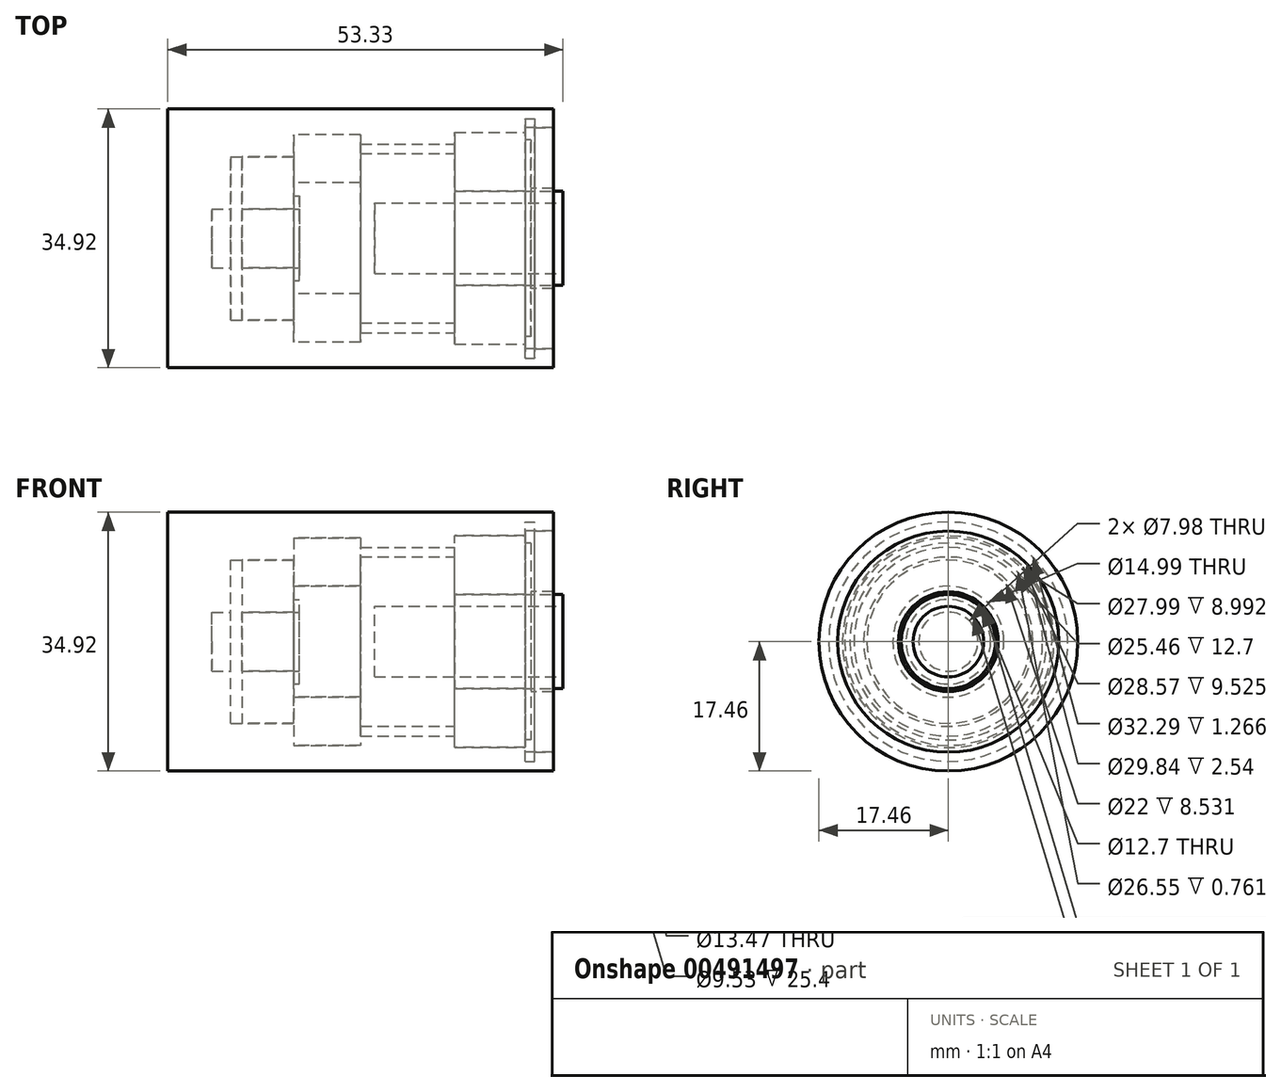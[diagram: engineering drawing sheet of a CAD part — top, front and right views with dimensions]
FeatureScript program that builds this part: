
annotation { "Feature Type Name" : "Feature", "Feature Type Description" : "" }
export const myFeature = defineFeature(function(context is Context, id is Id, definition is map)
    precondition{}
    {
        {
            var Q0;
            Q0=qCreatedBy(makeId("Front.planeOp"),FACE);
            var sketch = newSketch(context, id + "F0", { "sketchPlane" : qUnion([Q0])});
            skLineSegment(sketch, "E0.bottom", {"start": v(0, 0) * mm, "end": v(9.53, 0) * mm});
            skLineSegment(sketch, "E0.top", {"start": v(0, 14.29) * mm, "end": v(9.52, 14.29) * mm});
            skLineSegment(sketch, "E1.bottom", {"start": v(0, 0) * mm, "end": v(-12.7, 0) * mm});
            skLineSegment(sketch, "E1.top", {"start": v(0, 11.43) * mm, "end": v(-12.7, 11.43) * mm});
            skLineSegment(sketch, "E2.bottom", {"start": v(-12.7, 0) * mm, "end": v(-21.7, 0) * mm});
            skLineSegment(sketch, "E2.top", {"start": v(-12.7, 14) * mm, "end": v(-21.7, 14) * mm});
            skLineSegment(sketch, "E3.bottom", {"start": v(-21.7, 0) * mm, "end": v(-26.7, 0) * mm});
            skLineSegment(sketch, "E4.bottom", {"start": v(9.53, 0) * mm, "end": v(14.6, 0) * mm});
            skLineSegment(sketch, "E4.top", {"start": v(9.53, 6.35) * mm, "end": v(14.6, 6.35) * mm});
            skLineSegment(sketch, "E4.right", {"start": v(14.6, 0) * mm, "end": v(14.6, 6.35) * mm});
            skLineSegment(sketch, "E5", {"start": v(-12.7, 7.5) * mm, "end": v(-21.7, 7.5) * mm});
            skLineSegment(sketch, "E6", {"start": v(9.52, 14.29) * mm, "end": v(9.53, 6.35) * mm});
            skLineSegment(sketch, "E7", {"start": v(-12.7, 14) * mm, "end": v(-12.7, 7.5) * mm});
            skLineSegment(sketch, "E8", {"start": v(-21.7, 14) * mm, "end": v(-21.7, 3.99) * mm});
            skLineSegment(sketch, "E9", {"start": v(-27.69, 11) * mm, "end": v(-21.7, 11) * mm});
            skLineSegment(sketch, "E10", {"start": v(-26.7, 0) * mm, "end": v(-27.69, 0) * mm});
            skLineSegment(sketch, "E11", {"start": v(0, 14.29) * mm, "end": v(0, 6.35) * mm});
            skLineSegment(sketch, "E12", {"start": v(0, 6.35) * mm, "end": v(9.53, 6.35) * mm});
            skLineSegment(sketch, "E13", {"start": v(13.33, 7.5) * mm, "end": v(13.33, 17.46) * mm});
            skLineSegment(sketch, "E14", {"start": v(-32.78, 0) * mm, "end": v(-27.69, 0) * mm});
            skLineSegment(sketch, "E15", {"start": v(13.33, 17.46) * mm, "end": v(-37.47, 17.46) * mm});
            skLineSegment(sketch, "E16", {"start": v(-37.47, 0) * mm, "end": v(-32.78, 0) * mm});
            skLineSegment(sketch, "E17", {"start": v(-27.69, 11) * mm, "end": v(-30.22, 11) * mm});
            skLineSegment(sketch, "E18", {"start": v(-30.22, 0) * mm, "end": v(-27.69, 0) * mm});
            skLineSegment(sketch, "E19", {"start": v(13.33, 14.92) * mm, "end": v(10.8, 14.92) * mm});
            skLineSegment(sketch, "E20", {"start": v(10.8, 14.92) * mm, "end": v(10.8, 16.15) * mm});
            skLineSegment(sketch, "E21", {"start": v(10.8, 16.15) * mm, "end": v(9.52, 16.15) * mm});
            skLineSegment(sketch, "E22", {"start": v(9.52, 16.15) * mm, "end": v(9.52, 14.29) * mm});
            skLineSegment(sketch, "E23", {"start": v(9.52, 13.27) * mm, "end": v(10.29, 13.27) * mm});
            skLineSegment(sketch, "E24", {"start": v(10.29, 13.27) * mm, "end": v(10.29, 7.5) * mm});
            skLineSegment(sketch, "E25", {"start": v(13.33, 7.5) * mm, "end": v(13.33, 6.74) * mm});
            skLineSegment(sketch, "E26", {"start": v(13.33, 6.74) * mm, "end": v(10.29, 6.74) * mm});
            skLineSegment(sketch, "E27", {"start": v(10.29, 6.74) * mm, "end": v(10.29, 7.5) * mm});
            skLineSegment(sketch, "E28", {"start": v(0, 12.73) * mm, "end": v(-12.7, 12.73) * mm});
            skLineSegment(sketch, "E29", {"start": v(10.8, 14.92) * mm, "end": v(9.52, 14.92) * mm});
            skLineSegment(sketch, "E30", {"start": v(-21.7, 3.99) * mm, "end": v(-28.7, 3.99) * mm});
            skLineSegment(sketch, "E31", {"start": v(-28.7, 3.99) * mm, "end": v(-28.7, 11) * mm});
            skLineSegment(sketch, "E32", {"start": v(-28.7, 3.99) * mm, "end": v(-28.7, 0) * mm});
            skLineSegment(sketch, "E33", {"start": v(-21.7, 3.99) * mm, "end": v(-20.92, 3.99) * mm});
            skLineSegment(sketch, "E34", {"start": v(-20.92, 3.99) * mm, "end": v(-20.92, 5.71) * mm});
            skLineSegment(sketch, "E35", {"start": v(-20.92, 5.71) * mm, "end": v(-21.7, 5.71) * mm});
            skLineSegment(sketch, "E36", {"start": v(-30.22, 3.99) * mm, "end": v(-32.76, 3.99) * mm});
            skLineSegment(sketch, "E37", {"start": v(-32.76, 3.99) * mm, "end": v(-32.78, 0) * mm});
            skLineSegment(sketch, "E38", {"start": v(-30.22, 3.99) * mm, "end": v(-30.22, 11) * mm});
            skLineSegment(sketch, "E39", {"start": v(-37.47, 17.46) * mm, "end": v(-38.72, 17.46) * mm});
            skLineSegment(sketch, "E40", {"start": v(-38.72, 17.46) * mm, "end": v(-38.72, 0) * mm});
            skLineSegment(sketch, "E41", {"start": v(-37.47, 0) * mm, "end": v(-38.72, 0) * mm});
            skSolve(sketch);
        }
        {
            var Q0;
            Q0=makeQuery(id+"F0.imprint","IMPRINT",FACE,{"disambiguationData":[TD([[makeQuery(id+"F0.imprint","IMPRINT",EDGE,{"derivedFrom":sQuery(id+"F0.wireOp",EDGE,"E0.bottom")}),1.0]])]});
            var Q1;
            Q1=sQuery(id+"F0.wireOp",EDGE,"E3.bottom");
            revolve(context, id + "F1", {"entities" : qUnion([Q0]), "axis" : qUnion([Q1]), "revolveType" : RevolveType.FULL});
        }
        {
            var Q0;
            {var subQ3=sQuery(id+"F0.wireOp",EDGE,"E0.top");Q0=makeQuery(id+"F0.imprint","IMPRINT",FACE,{"disambiguationData":[TD([[makeQuery(id+"F0.imprint","IMPRINT",EDGE,{"derivedFrom":subQ3}),-1.0]])]});}
            var Q1;
            {var subQ3=sQuery(id+"F0.wireOp",EDGE,"E2.top");Q1=makeQuery(id+"F0.imprint","IMPRINT",FACE,{"disambiguationData":[TD([[makeQuery(id+"F0.imprint","IMPRINT",EDGE,{"derivedFrom":subQ3}),1.0]])]});}
            var Q2;
            {var subQ1=sQuery(id+"F0.wireOp",EDGE,"U3DAEwCZ-hZwE-VyH9-W5jA-IGdN1AD25CXx");Q2=makeQuery(id+"F0.imprint","IMPRINT",FACE,{"disambiguationData":[TD([[makeQuery(id+"F0.imprint","IMPRINT",EDGE,{"derivedFrom":subQ1}),-1.0]])]});}
            var Q3;
            Q3=makeQuery(id+"F1.opRevolve","SWEPT_EDGE",EDGE,{"disambiguationData":[OSD([sQuery(id+"F0.wireOp",EDGE,"E11"),sQuery(id+"F0.wireOp",EDGE,"E12")])]});
            revolve(context, id + "F2", {"entities" : qUnion([Q0, Q1, Q2]), "axis" : qUnion([Q3]), "revolveType" : RevolveType.FULL});
        }
        {
            var Q0;
            Q0=makeQuery(id+"F1.opRevolve","SWEPT_FACE",FACE,{"disambiguationData":[OSD([sQuery(id+"F0.wireOp",EDGE,"E4.right")])]});
            var sketch = newSketch(context, id + "F3", { "sketchPlane" : qUnion([Q0])});
            skCircle(sketch, "E42", {"center": v(0, 0) * mm, "radius": 4.76 * mm});
            skSolve(sketch);
        }
        {
            var Q0;
            Q0=makeQuery(id+"F3.imprint","IMPRINT",FACE,{"disambiguationData":[TD([[makeQuery(id+"F3.imprint","IMPRINT",EDGE,{"derivedFrom":sQuery(id+"F3.wireOp",EDGE,"E42")}),1.0]])]});
            extrude(context, id + "F4", {"entities" : qUnion([Q0]), "operationType" : NewBodyOperationType.REMOVE, "oppositeDirection" : true, "depth" : 25.4 * mm});
        }
        {
            var Q0;
            {var subQ7=sQuery(id+"F0.wireOp",EDGE,"E0.top");Q0=makeQuery(id+"F0.imprint","IMPRINT",FACE,{"disambiguationData":[TD([[makeQuery(id+"F0.imprint","IMPRINT",EDGE,{"derivedFrom":subQ7}),1.0]])]});}
            var Q1;
            Q1=makeQuery(id+"F2.opRevolve","SWEPT_FACE",FACE,{"disambiguationData":[OSD([sQuery(id+"F0.wireOp",EDGE,"E2.top")])]});
            revolve(context, id + "F5", {"entities" : qUnion([Q0]), "axis" : qUnion([Q1]), "revolveType" : RevolveType.FULL});
        }
        {
            var Q0;
            {var subQ5=sQuery(id+"F0.wireOp",EDGE,"E19");Q0=makeQuery(id+"F0.imprint","IMPRINT",FACE,{"disambiguationData":[TD([[makeQuery(id+"F0.imprint","IMPRINT",EDGE,{"derivedFrom":subQ5}),1.0]])]});}
            var Q1;
            Q1=makeQuery(id+"F1.opRevolve","SWEPT_FACE",FACE,{"disambiguationData":[OSD([sQuery(id+"F0.wireOp",EDGE,"E4.top"),sQuery(id+"F0.wireOp",EDGE,"E12")])]});
            revolve(context, id + "F6", {"entities" : qUnion([Q0]), "axis" : qUnion([Q1]), "revolveType" : RevolveType.FULL});
        }
        {
            var Q0;
            {var subQ1=sQuery(id+"F0.wireOp",EDGE,"E9");Q0=makeQuery(id+"F0.imprint","IMPRINT",FACE,{"disambiguationData":[TD([[makeQuery(id+"F0.imprint","IMPRINT",EDGE,{"derivedFrom":subQ1}),-1.0]])]});}
            var Q1;
            Q1=makeQuery(id+"F5.opRevolve","SWEPT_FACE",FACE,{"disambiguationData":[OSD([sQuery(id+"F0.wireOp",EDGE,"E15")])]});
            revolve(context, id + "F7", {"entities" : qUnion([Q0]), "axis" : qUnion([Q1]), "revolveType" : RevolveType.FULL});
        }
    });
